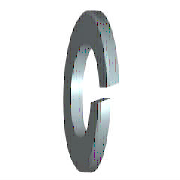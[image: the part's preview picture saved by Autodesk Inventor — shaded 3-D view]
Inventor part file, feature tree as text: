
AUTODESK INVENTOR PART (.ipt)
format: ipt  version: 2021 (Build 250183000, 183)  size: 126,976 bytes
history: native  units: mm (DEFAULTED — no unit token found)
features: sketch x2, extrude x1, other x1, plane x1
ambient origin geometry x6: Origin, YZ Plane, X Axis, Y Axis, Z Axis, Center Point
bodies: Solid1 (feature_tree), Body (feature_tree)
feature tree (5):
  extrude  "Cut"  Depth=14.9mm
  other  "Work Axis1"
  plane  "Work Plane1"
  sketch  "Sketch1"  dims[d0=8.2mm d1=14.9mm]
  sketch  "Sketch2"  dims[d2=2.1mm d3=0.0mm d4=0.42mm d5=0.42mm d6=12.217305mm d7=2.1mm d8=0.0mm d9=0.0mm d10=0.0mm d11=0.0mm d12=0.0mm]
